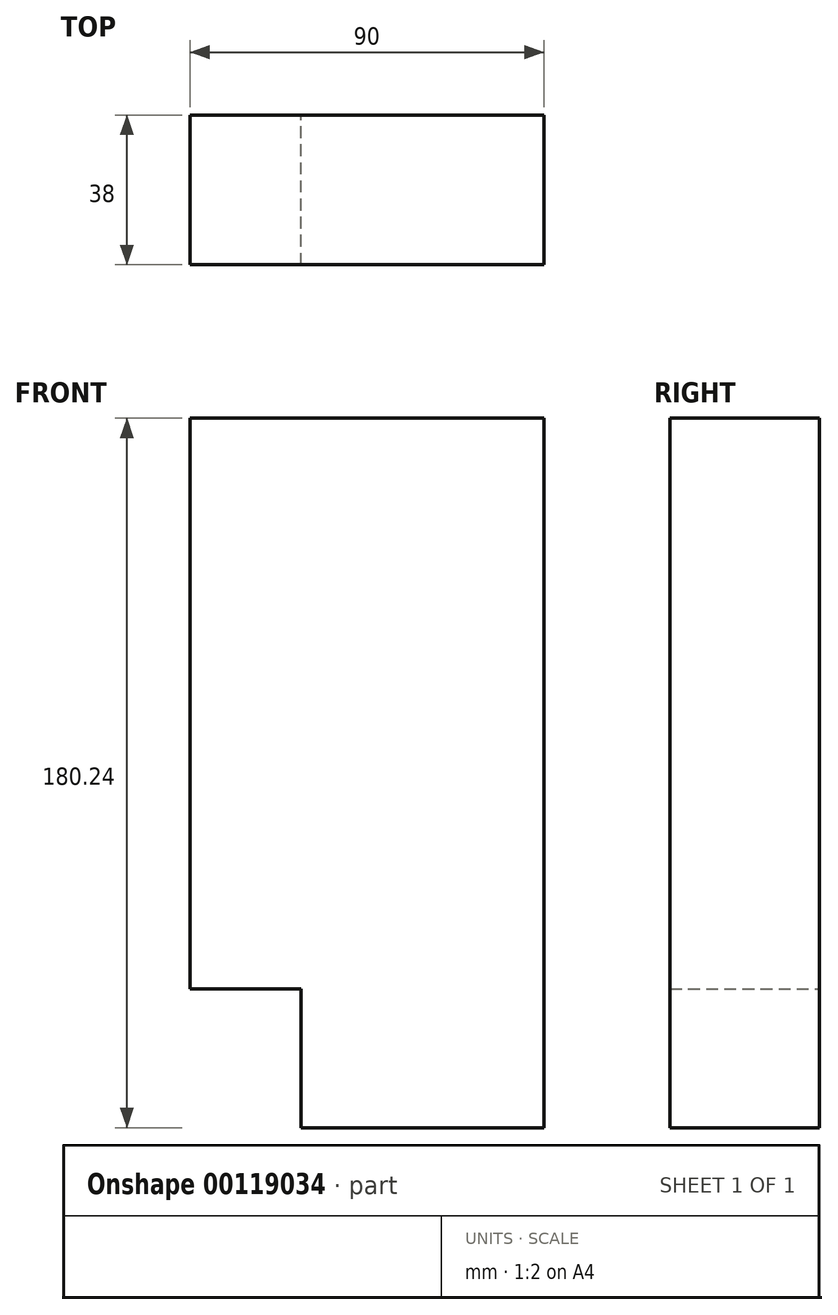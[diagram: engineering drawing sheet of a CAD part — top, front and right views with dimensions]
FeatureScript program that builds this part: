
annotation { "Feature Type Name" : "Feature", "Feature Type Description" : "" }
export const myFeature = defineFeature(function(context is Context, id is Id, definition is map)
    precondition{}
    {
        {
            var Q0;
            Q0=qCreatedBy(makeId("Front.planeOp"),FACE);
            var sketch = newSketch(context, id + "F0", { "sketchPlane" : qUnion([Q0])});
            skLineSegment(sketch, "E0", {"start": v(-14.43, 118.74) * mm, "end": v(-14.43, -26.26) * mm});
            skLineSegment(sketch, "E1", {"start": v(-14.43, -26.26) * mm, "end": v(13.78, -26.26) * mm});
            skLineSegment(sketch, "E2", {"start": v(13.78, -26.26) * mm, "end": v(13.78, -61.5) * mm});
            skLineSegment(sketch, "E3", {"start": v(13.78, -61.5) * mm, "end": v(75.57, -61.5) * mm});
            skLineSegment(sketch, "E4", {"start": v(75.57, -61.5) * mm, "end": v(75.57, -29.64) * mm});
            skLineSegment(sketch, "E5", {"start": v(75.57, -29.64) * mm, "end": v(75.57, 118.74) * mm});
            skLineSegment(sketch, "E6", {"start": v(75.57, 118.74) * mm, "end": v(-14.43, 118.74) * mm});
            skSolve(sketch);
        }
        {
            var Q0;
            Q0 = qSketchRegion(id + "F0", true);
            extrude(context, id + "F1", {"entities" : qUnion([Q0]), "depth" : 38 * mm});
        }
    });
